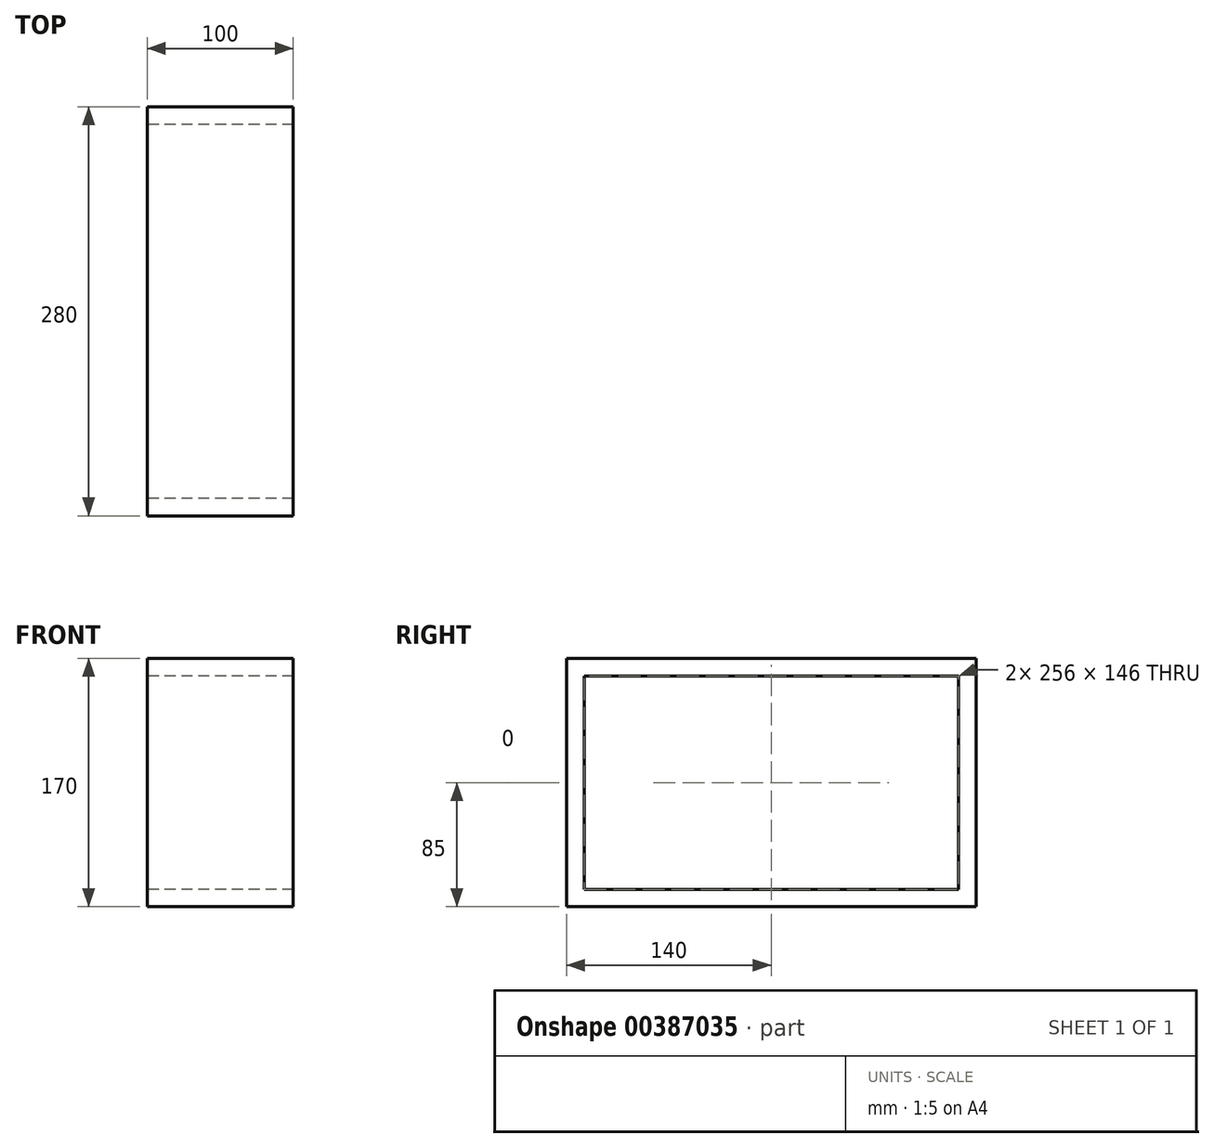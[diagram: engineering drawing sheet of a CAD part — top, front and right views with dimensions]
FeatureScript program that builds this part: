
annotation { "Feature Type Name" : "Feature", "Feature Type Description" : "" }
export const myFeature = defineFeature(function(context is Context, id is Id, definition is map)
    precondition{}
    {
        {
            var Q0;
            Q0=qCreatedBy(makeId("Right.planeOp"),FACE);
            var sketch = newSketch(context, id + "F0", { "sketchPlane" : qUnion([Q0])});
            skLineSegment(sketch, "E0", {"start": v(0, 0) * mm, "end": v(0, 47.95) * mm});
            skLineSegment(sketch, "E1.bottom", {"start": v(-140, 85) * mm, "end": v(140, 85) * mm});
            skLineSegment(sketch, "E1.top", {"start": v(-140, -85) * mm, "end": v(140, -85) * mm});
            skLineSegment(sketch, "E1.left", {"start": v(-140, 85) * mm, "end": v(-140, -85) * mm});
            skLineSegment(sketch, "E1.right", {"start": v(140, 85) * mm, "end": v(140, -85) * mm});
            skPoint(sketch, "E1.middle", {"position": v(0, 0) * mm});
            skLineSegment(sketch, "E2.bottom", {"start": v(-86.5, 54.5) * mm, "end": v(86.5, 54.5) * mm});
            skLineSegment(sketch, "E2.top", {"start": v(-86.5, -54.5) * mm, "end": v(86.5, -54.5) * mm});
            skLineSegment(sketch, "E2.left", {"start": v(-86.5, 54.5) * mm, "end": v(-86.5, -54.5) * mm});
            skLineSegment(sketch, "E2.right", {"start": v(86.5, 54.5) * mm, "end": v(86.5, -54.5) * mm});
            skLineSegment(sketch, "E3.0", {"start": v(-128, 73) * mm, "end": v(128, 73) * mm});
            skLineSegment(sketch, "E3.1", {"start": v(-128, 73) * mm, "end": v(-128, -73) * mm});
            skLineSegment(sketch, "E3.2", {"start": v(-128, -73) * mm, "end": v(128, -73) * mm});
            skLineSegment(sketch, "E3.3", {"start": v(128, 73) * mm, "end": v(128, -73) * mm});
            skSolve(sketch);
        }
        {
            var Q0;
            Q0=makeQuery(id+"F0.imprint","IMPRINT",FACE,{"disambiguationData":[TD([[makeQuery(id+"F0.imprint","IMPRINT",EDGE,{"derivedFrom":sQuery(id+"F0.wireOp",EDGE,"E1.bottom")}),-1.0]])]});
            extrude(context, id + "F1", {"entities" : qUnion([Q0]), "depth" : 100 * mm});
        }
    });
